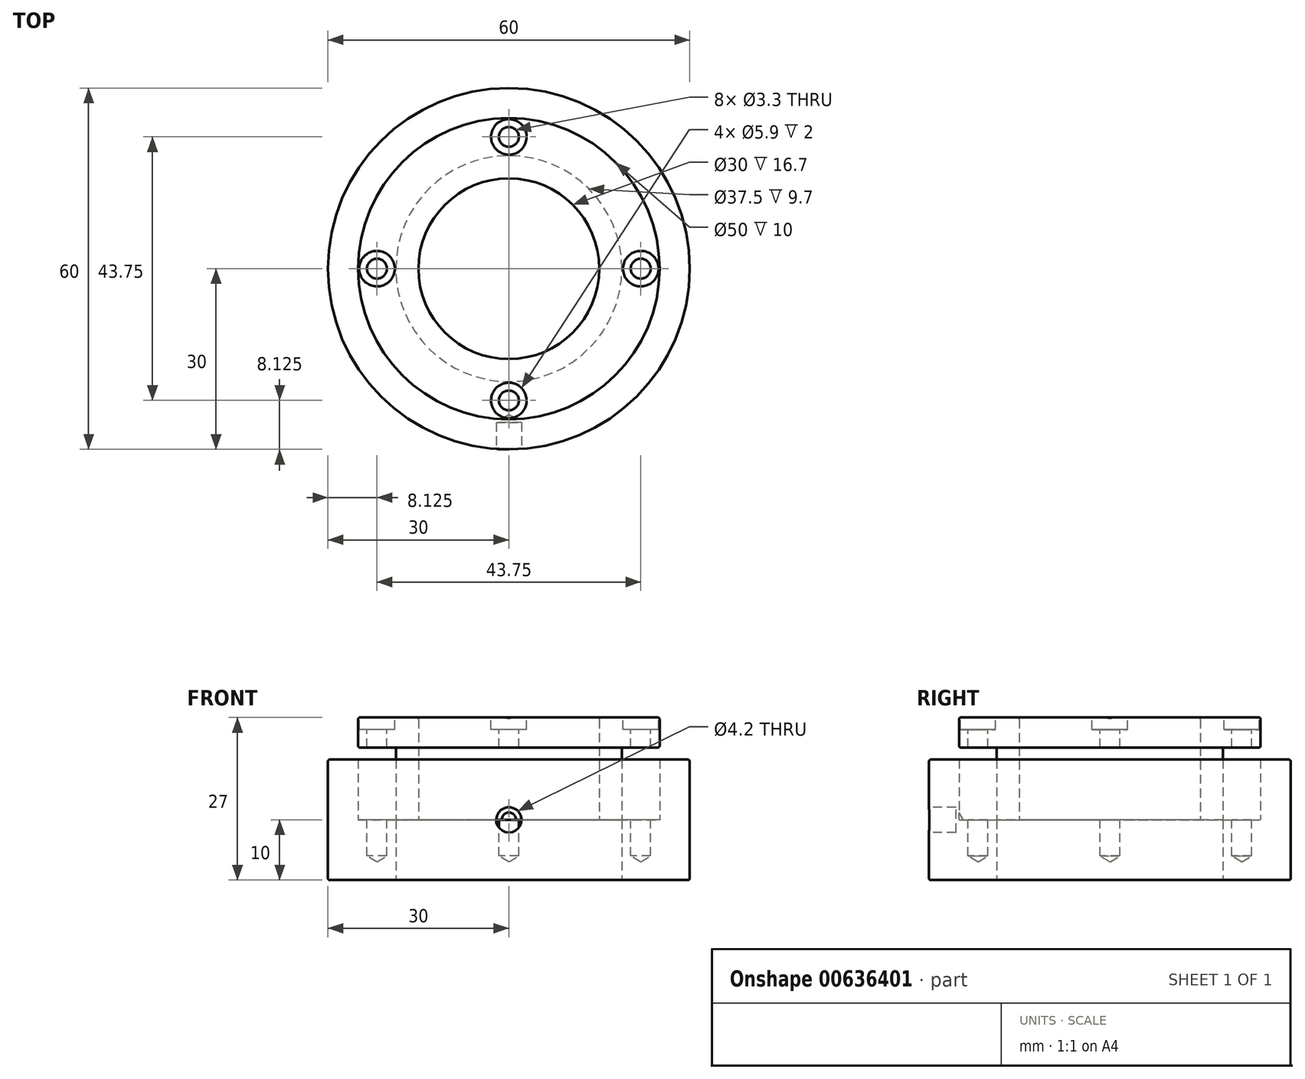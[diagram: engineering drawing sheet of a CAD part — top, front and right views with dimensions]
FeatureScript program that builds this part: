
annotation { "Feature Type Name" : "Feature", "Feature Type Description" : "" }
export const myFeature = defineFeature(function(context is Context, id is Id, definition is map)
    precondition{}
    {
        {
            var Q0;
            Q0=qCreatedBy(makeId("Top.planeOp"),FACE);
            var sketch = newSketch(context, id + "F0", { "sketchPlane" : qUnion([Q0])});
            skCircle(sketch, "E0", {"center": v(0, 0) * mm, "radius": 30 * mm});
            skCircle(sketch, "E1", {"center": v(0, 0) * mm, "radius": 18.75 * mm});
            skCircle(sketch, "E2", {"center": v(0, 0) * mm, "radius": 15 * mm});
            skCircle(sketch, "E3", {"center": v(0, 0) * mm, "radius": 25 * mm});
            skSolve(sketch);
        }
        {
            var Q0;
            Q0=makeQuery(id+"F0.imprint","IMPRINT",FACE,{"disambiguationData":[TD([[makeQuery(id+"F0.imprint","IMPRINT",EDGE,{"derivedFrom":sQuery(id+"F0.wireOp",EDGE,"E0")}),1.0]])]});
            var Q1;
            Q1=makeQuery(id+"F0.imprint","IMPRINT",FACE,{"disambiguationData":[TD([[makeQuery(id+"F0.imprint","IMPRINT",EDGE,{"derivedFrom":sQuery(id+"F0.wireOp",EDGE,"E1")}),-1.0]])]});
            extrude(context, id + "F1", {"entities" : qUnion([Q0, Q1]), "endBound" : BoundingType.SYMMETRIC, "depth" : 20 * mm, "offsetDistance" : 25 * mm, "hasSecondDirectionDraft" : true, "secondDirectionDraftAngle" : 3 * degree});
        }
        {
            var Q0;
            Q0=makeQuery(id+"F0.imprint","IMPRINT",FACE,{"disambiguationData":[TD([[makeQuery(id+"F0.imprint","IMPRINT",EDGE,{"derivedFrom":sQuery(id+"F0.wireOp",EDGE,"E1")}),1.0]])]});
            var Q1;
            Q1=makeQuery(id+"F0.imprint","IMPRINT",FACE,{"disambiguationData":[TD([[makeQuery(id+"F0.imprint","IMPRINT",EDGE,{"derivedFrom":sQuery(id+"F0.wireOp",EDGE,"E2")}),1.0]])]});
            extrude(context, id + "F2", {"entities" : qUnion([Q0, Q1]), "endBound" : BoundingType.SYMMETRIC, "depth" : 0 * mm, "offsetDistance" : 25 * mm});
        }
        {
            var Q0;
            Q0=qCreatedBy(makeId("Front.planeOp"),FACE);
            cPlane(context, id + "F3", {"entities" : qUnion([Q0]), "cplaneType" : CPlaneType.OFFSET, "offset" : 30 * mm, "width" : 150 * mm, "height" : 150 * mm});
        }
        {
            var Q0;
            Q0=qCreatedBy(id+"F3.planeOp",FACE);
            var sketch = newSketch(context, id + "F4", { "sketchPlane" : qUnion([Q0])});
            skPoint(sketch, "E4", {"position": v(0, 0) * mm});
            skSolve(sketch);
        }
        {
            var Q0;
            Q0=sQuery(id+"F4.wireOp",VERTEX,"E4");
            var Q1;
            Q1=makeQuery(id+"F1.opExtrude","SWEPT_BODY",BODY,{"disambiguationData":[OSD([sQuery(id+"F0.wireOp",EDGE,"E0"),sQuery(id+"F0.wireOp",EDGE,"E1")])]});
            hole(context, id + "F5", {"style" : HoleStyle.SIMPLE, "endStyle" : HoleEndStyle.BLIND, "standardTappedOrClearance" : lookupTablePath({ "standard" : "ISO", "engagement" : "75%", "pitch" : "0.8 mm", "size" : "M5", "type" : "Tapped" }), "standardBlindInLast" : lookupTablePath({ "standard" : "ISO", "engagement" : "75%", "pitch" : "0.8 mm", "size" : "M5", "type" : "Tapped" }), "holeDiameter" : 4.2 * mm, "majorDiameter" : 5 * mm, "showTappedDepth" : true, "holeDepth" : 4.4 * mm, "isTappedThrough" : true, "tappedDepth" : 2 * mm, "tapClearance" : 3, "locations" : qUnion([Q0]), "scope" : qUnion([Q1])});
        }
        {
            var Q0;
            Q0=makeQuery(id+"F0.imprint","IMPRINT",FACE,{"disambiguationData":[TD([[makeQuery(id+"F0.imprint","IMPRINT",EDGE,{"derivedFrom":sQuery(id+"F0.wireOp",EDGE,"E1")}),-1.0]])]});
            var Q1;
            Q1=makeQuery(id+"F0.imprint","IMPRINT",FACE,{"disambiguationData":[TD([[makeQuery(id+"F0.imprint","IMPRINT",EDGE,{"derivedFrom":sQuery(id+"F0.wireOp",EDGE,"E1")}),1.0]])]});
            extrude(context, id + "F6", {"entities" : qUnion([Q0, Q1]), "depth" : 17 * mm, "offsetDistance" : 25 * mm});
        }
        {
            var Q0;
            Q0=makeQuery(id+"F0.imprint","IMPRINT",FACE,{"disambiguationData":[TD([[makeQuery(id+"F0.imprint","IMPRINT",EDGE,{"derivedFrom":sQuery(id+"F0.wireOp",EDGE,"E1")}),-1.0]])]});
            extrude(context, id + "F7", {"entities" : qUnion([Q0]), "operationType" : NewBodyOperationType.REMOVE, "depth" : 12 * mm, "offsetDistance" : 25 * mm});
        }
        {
            var Q0;
            Q0=makeQuery(id+"F6.opExtrude","CAP_FACE",FACE,{"disambiguationData":[OSD([sQuery(id+"F0.wireOp",EDGE,"E2"),sQuery(id+"F0.wireOp",EDGE,"E3")])],"isStart":false});
            var sketch = newSketch(context, id + "F8", { "sketchPlane" : qUnion([Q0])});
            skPoint(sketch, "E5", {"position": v(0, -21.88) * mm});
            skPoint(sketch, "E6", {"position": v(21.88, 0) * mm});
            skPoint(sketch, "E7", {"position": v(0, 21.88) * mm});
            skPoint(sketch, "E8", {"position": v(-21.88, 0) * mm});
            skCircle(sketch, "E9", {"center": v(0, 0) * mm, "radius": 21.88 * mm, "construction": true});
            skSolve(sketch);
        }
        {
            var Q0;
            Q0=sQuery(id+"F8.wireOp",VERTEX,"E8");
            var Q1;
            Q1=sQuery(id+"F8.wireOp",VERTEX,"E7");
            var Q2;
            Q2=sQuery(id+"F8.wireOp",VERTEX,"E6");
            var Q3;
            Q3=sQuery(id+"F8.wireOp",VERTEX,"E5");
            var Q4;
            Q4=makeQuery(id+"F6.opExtrude","SWEPT_BODY",BODY,{"disambiguationData":[OSD([sQuery(id+"F0.wireOp",EDGE,"E2"),sQuery(id+"F0.wireOp",EDGE,"E3")])]});
            hole(context, id + "F9", {"style" : HoleStyle.C_BORE, "endStyle" : HoleEndStyle.THROUGH, "holeDiameter" : 3.3 * mm, "cBoreDiameter" : 5.9 * mm, "cBoreDepth" : 2 * mm, "majorDiameter" : 4 * mm, "isTappedThrough" : true, "tappedDepth" : 2 * mm, "tapClearance" : 3, "locations" : qUnion([Q0, Q1, Q2, Q3]), "scope" : qUnion([Q4])});
        }
        {
            var Q0;
            Q0=makeQuery(id+"F1.opExtrude","CAP_FACE",FACE,{"disambiguationData":[OSD([sQuery(id+"F0.wireOp",EDGE,"E0"),sQuery(id+"F0.wireOp",EDGE,"E1")])],"isStart":false});
            var sketch = newSketch(context, id + "F10", { "sketchPlane" : qUnion([Q0])});
            skPoint(sketch, "E10", {"position": v(0, -21.88) * mm});
            skPoint(sketch, "E11", {"position": v(21.88, 0) * mm});
            skPoint(sketch, "E12", {"position": v(0, 21.88) * mm});
            skPoint(sketch, "E13", {"position": v(-21.88, 0) * mm});
            skCircle(sketch, "E14", {"center": v(0, 0) * mm, "radius": 21.88 * mm, "construction": true});
            skSolve(sketch);
        }
        {
            var Q0;
            Q0=sQuery(id+"F10.wireOp",VERTEX,"E13");
            var Q1;
            Q1=sQuery(id+"F10.wireOp",VERTEX,"E12");
            var Q2;
            Q2=sQuery(id+"F10.wireOp",VERTEX,"E11");
            var Q3;
            Q3=sQuery(id+"F10.wireOp",VERTEX,"E10");
            var Q4;
            Q4=makeQuery(id+"F1.opExtrude","SWEPT_BODY",BODY,{"disambiguationData":[OSD([sQuery(id+"F0.wireOp",EDGE,"E0"),sQuery(id+"F0.wireOp",EDGE,"E1")])]});
            hole(context, id + "F11", {"style" : HoleStyle.SIMPLE, "endStyle" : HoleEndStyle.BLIND, "standardTappedOrClearance" : lookupTablePath({ "standard" : "ISO", "fit" : "Normal", "size" : "M3", "type" : "Clearance" }), "standardBlindInLast" : lookupTablePath({ "fit" : "Standard", "standard" : "ISO", "size" : "M3", "type" : "Clearance" }), "holeDiameter" : 3.3 * mm, "majorDiameter" : 5 * mm, "holeDepth" : 6 * mm, "isTappedThrough" : true, "tappedDepth" : 2 * mm, "tapClearance" : 3, "locations" : qUnion([Q0, Q1, Q2, Q3]), "scope" : qUnion([Q4])});
        }
        {
            var Q0;
            Q0=makeQuery(id+"F1.opExtrude","CAP_EDGE",EDGE,{"disambiguationData":[OSD([sQuery(id+"F0.wireOp",EDGE,"E0")])],"isStart":false});
            var Q1;
            Q1=makeQuery(id+"F1.opExtrude","CAP_EDGE",EDGE,{"disambiguationData":[OSD([sQuery(id+"F0.wireOp",EDGE,"E0")])],"isStart":true});
            var Q2;
            Q2=makeQuery(id+"F6.opExtrude","SWEPT_FACE",FACE,{"disambiguationData":[OSD([sQuery(id+"F0.wireOp",EDGE,"E3")])]});
            var Q3;
            Q3=makeQuery(id+"F6.opExtrude","CAP_EDGE",EDGE,{"disambiguationData":[OSD([sQuery(id+"F0.wireOp",EDGE,"E2")])],"isStart":false});
            var Q4;
            Q4=makeQuery(id+"F2.opExtrude","CAP_EDGE",EDGE,{"disambiguationData":[OSD([sQuery(id+"F0.wireOp",EDGE,"E1")])],"isStart":true});
            var Q5;
            Q5=makeQuery(id+"F1.opExtrude","CAP_EDGE",EDGE,{"disambiguationData":[OSD([sQuery(id+"F0.wireOp",EDGE,"E1")])],"isStart":true});
            fillet(context, id + "F12", {"entities" : qUnion([Q0, Q1, Q2, Q3, Q4, Q5]), "radius" : 0.3 * mm, "tangentPropagation" : true, "allowEdgeOverflow" : false});
        }
    });
